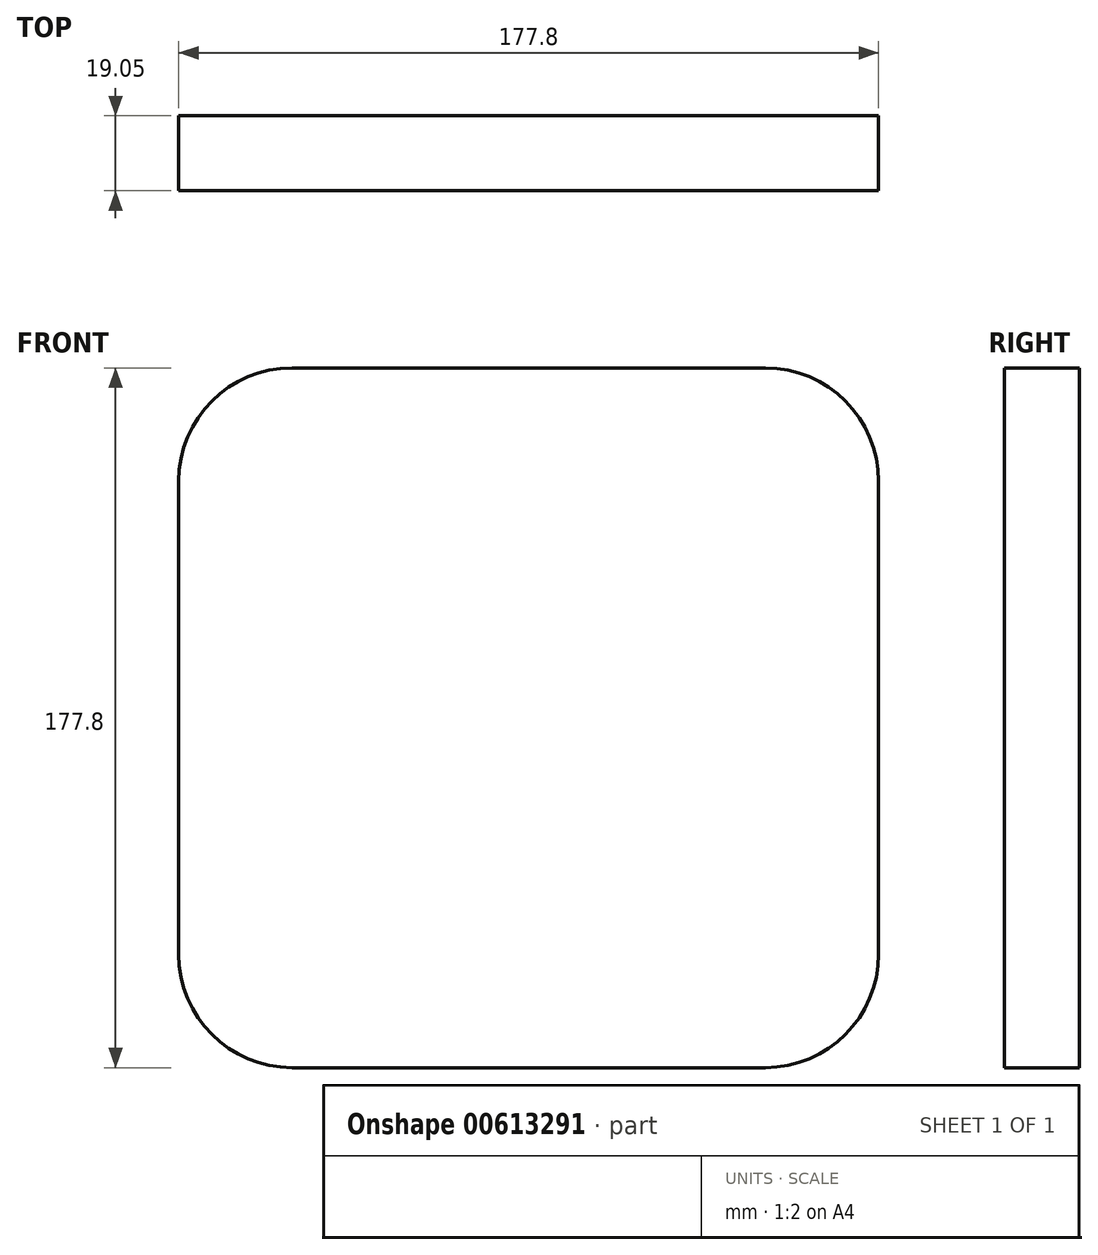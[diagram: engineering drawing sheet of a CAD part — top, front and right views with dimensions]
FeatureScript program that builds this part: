
annotation { "Feature Type Name" : "Feature", "Feature Type Description" : "" }
export const myFeature = defineFeature(function(context is Context, id is Id, definition is map)
    precondition{}
    {
        {
            var Q0;
            Q0=qCreatedBy(makeId("Front.planeOp"),FACE);
            var sketch = newSketch(context, id + "F0", { "sketchPlane" : qUnion([Q0])});
            skLineSegment(sketch, "E0.bottom", {"start": v(28.78, 0) * mm, "end": v(149.02, 0) * mm});
            skLineSegment(sketch, "E0.top", {"start": v(28.78, 177.8) * mm, "end": v(149.02, 177.8) * mm});
            skLineSegment(sketch, "E0.left", {"start": v(0, 28.78) * mm, "end": v(0, 149.02) * mm});
            skLineSegment(sketch, "E0.right", {"start": v(177.8, 28.78) * mm, "end": v(177.8, 149.02) * mm});
            skPoint(sketch, "E1.visualSharp", {"position": v(0, 177.8) * mm});
            skArc(sketch, "E1.filletArc", {"start": v(28.78, 177.8) * mm, "mid": v(8.43, 169.37) * mm, "end": v(0, 149.02) * mm});
            skPoint(sketch, "E2.visualSharp", {"position": v(177.8, 177.8) * mm});
            skArc(sketch, "E2.filletArc", {"start": v(177.8, 149.02) * mm, "mid": v(169.37, 169.37) * mm, "end": v(149.02, 177.8) * mm});
            skPoint(sketch, "E3.visualSharp", {"position": v(177.8, 0) * mm});
            skArc(sketch, "E3.filletArc", {"start": v(149.02, 0) * mm, "mid": v(169.37, 8.43) * mm, "end": v(177.8, 28.78) * mm});
            skPoint(sketch, "E4.visualSharp", {"position": v(0, 0) * mm});
            skArc(sketch, "E4.filletArc", {"start": v(0, 28.78) * mm, "mid": v(8.43, 8.43) * mm, "end": v(28.78, 0) * mm});
            skSolve(sketch);
        }
        {
            var Q0;
            Q0=makeQuery(id+"F0.imprint","IMPRINT",FACE,{"disambiguationData":[TD([[makeQuery(id+"F0.imprint","IMPRINT",EDGE,{"derivedFrom":sQuery(id+"F0.wireOp",EDGE,"1qnOmSaI-Xxrh-0afN-UeiG-LIwPmX5NAdLk.bottom")}),1.0]])]});
            var Q1;
            Q1=makeQuery(id+"F0.imprint","IMPRINT",FACE,{"disambiguationData":[TD([[makeQuery(id+"F0.imprint","IMPRINT",EDGE,{"derivedFrom":sQuery(id+"F0.wireOp",EDGE,"4ba0bba3-8742-4700-8735-c76f5317d59b.0.1.0")}),1.0]])]});
            var Q2;
            Q2=makeQuery(id+"F0.imprint","IMPRINT",FACE,{"disambiguationData":[TD([[makeQuery(id+"F0.imprint","IMPRINT",EDGE,{"derivedFrom":sQuery(id+"F0.wireOp",EDGE,"4ba0bba3-8742-4700-8735-c76f5317d59b.1.1.0")}),1.0]])]});
            var Q3;
            Q3=makeQuery(id+"F0.imprint","IMPRINT",FACE,{"disambiguationData":[TD([[makeQuery(id+"F0.imprint","IMPRINT",EDGE,{"derivedFrom":sQuery(id+"F0.wireOp",EDGE,"4ba0bba3-8742-4700-8735-c76f5317d59b.1.0.0")}),1.0]])]});
            var Q4;
            Q4=makeQuery(id+"F0.imprint","IMPRINT",FACE,{"disambiguationData":[TD([[makeQuery(id+"F0.imprint","IMPRINT",EDGE,{"derivedFrom":sQuery(id+"F0.wireOp",EDGE,"E0.bottom")}),1.0]])]});
            var Q5;
            Q5=makeQuery(id+"F0.imprint","IMPRINT",FACE,{"disambiguationData":[TD([[makeQuery(id+"F0.imprint","IMPRINT",EDGE,{"derivedFrom":sQuery(id+"F0.wireOp",EDGE,"bJ1m94SH-JbWV-fS9y-Xvgq-A2zdKJ9BKWsM")}),1.0]])]});
            extrude(context, id + "F1", {"entities" : qUnion([Q0, Q1, Q2, Q3, Q4, Q5]), "depth" : 19.05 * mm, "offsetDistance" : 25.4 * mm});
        }
    });
